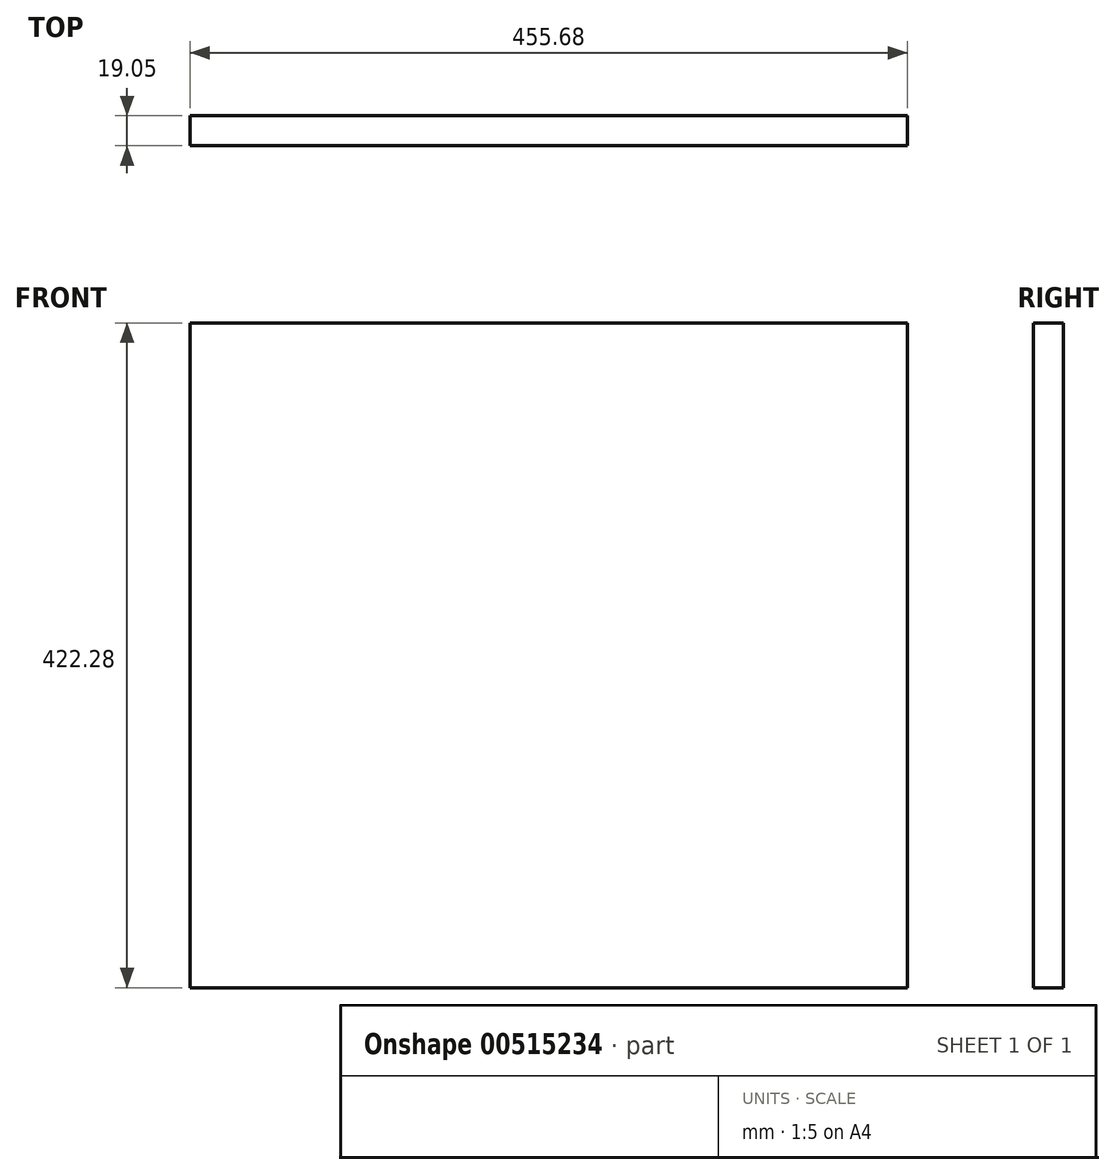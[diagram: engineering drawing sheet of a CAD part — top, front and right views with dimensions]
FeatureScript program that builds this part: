
annotation { "Feature Type Name" : "Feature", "Feature Type Description" : "" }
export const myFeature = defineFeature(function(context is Context, id is Id, definition is map)
    precondition{}
    {
        {
            var Q0;
            Q0=qCreatedBy(makeId("Front.planeOp"),FACE);
            var sketch = newSketch(context, id + "F0", { "sketchPlane" : qUnion([Q0])});
            skLineSegment(sketch, "E0.left", {"start": v(-457.2, 198.44) * mm, "end": v(-457.2, -198.44) * mm});
            skPoint(sketch, "E0.middle", {"position": v(0, 0) * mm});
            skLineSegment(sketch, "E1", {"start": v(-457.2, 198.44) * mm, "end": v(-1.52, 198.44) * mm});
            skLineSegment(sketch, "E2", {"start": v(-1.52, 198.44) * mm, "end": v(-1.52, -198.44) * mm});
            skPoint(sketch, "E2.endSnap0", {"position": v(0, -198.44) * mm});
            skLineSegment(sketch, "E3", {"start": v(-1.52, -198.44) * mm, "end": v(1.65, -198.44) * mm});
            skLineSegment(sketch, "E4", {"start": v(1.65, -198.44) * mm, "end": v(1.65, 198.44) * mm});
            skPoint(sketch, "E4.endSnap0", {"position": v(0, 198.44) * mm});
            skLineSegment(sketch, "E5.top", {"start": v(-457.2, -198.44) * mm, "end": v(-1.52, -198.44) * mm});
            skSolve(sketch);
        }
        {
            var Q0;
            Q0=makeQuery(id+"F0.imprint","IMPRINT",FACE,{"disambiguationData":[TD([[makeQuery(id+"F0.imprint","IMPRINT",EDGE,{"derivedFrom":sQuery(id+"F0.wireOp",EDGE,"E1")}),-1.0]])]});
            var Q1;
            Q1=makeQuery(id+"F0.imprint","IMPRINT",FACE,{"disambiguationData":[TD([[makeQuery(id+"F0.imprint","IMPRINT",EDGE,{"derivedFrom":sQuery(id+"F0.wireOp",EDGE,"goDqZllA-siS4-IZkI-TRe5-aVMxi5cb2Uoc.bottom")}),1.0]])]});
            extrude(context, id + "F1", {"entities" : qUnion([Q0, Q1]), "depth" : 19.05 * mm});
        }
        {
            var Q0;
            Q0=makeQuery(id+"F1.opExtrude","SWEPT_FACE",FACE,{"disambiguationData":[OSD([sQuery(id+"F0.wireOp",EDGE,"E1")])]});
            extrude(context, id + "F2", {"entities" : qUnion([Q0]), "operationType" : NewBodyOperationType.ADD, "depth" : 25.4 * mm});
        }
    });
